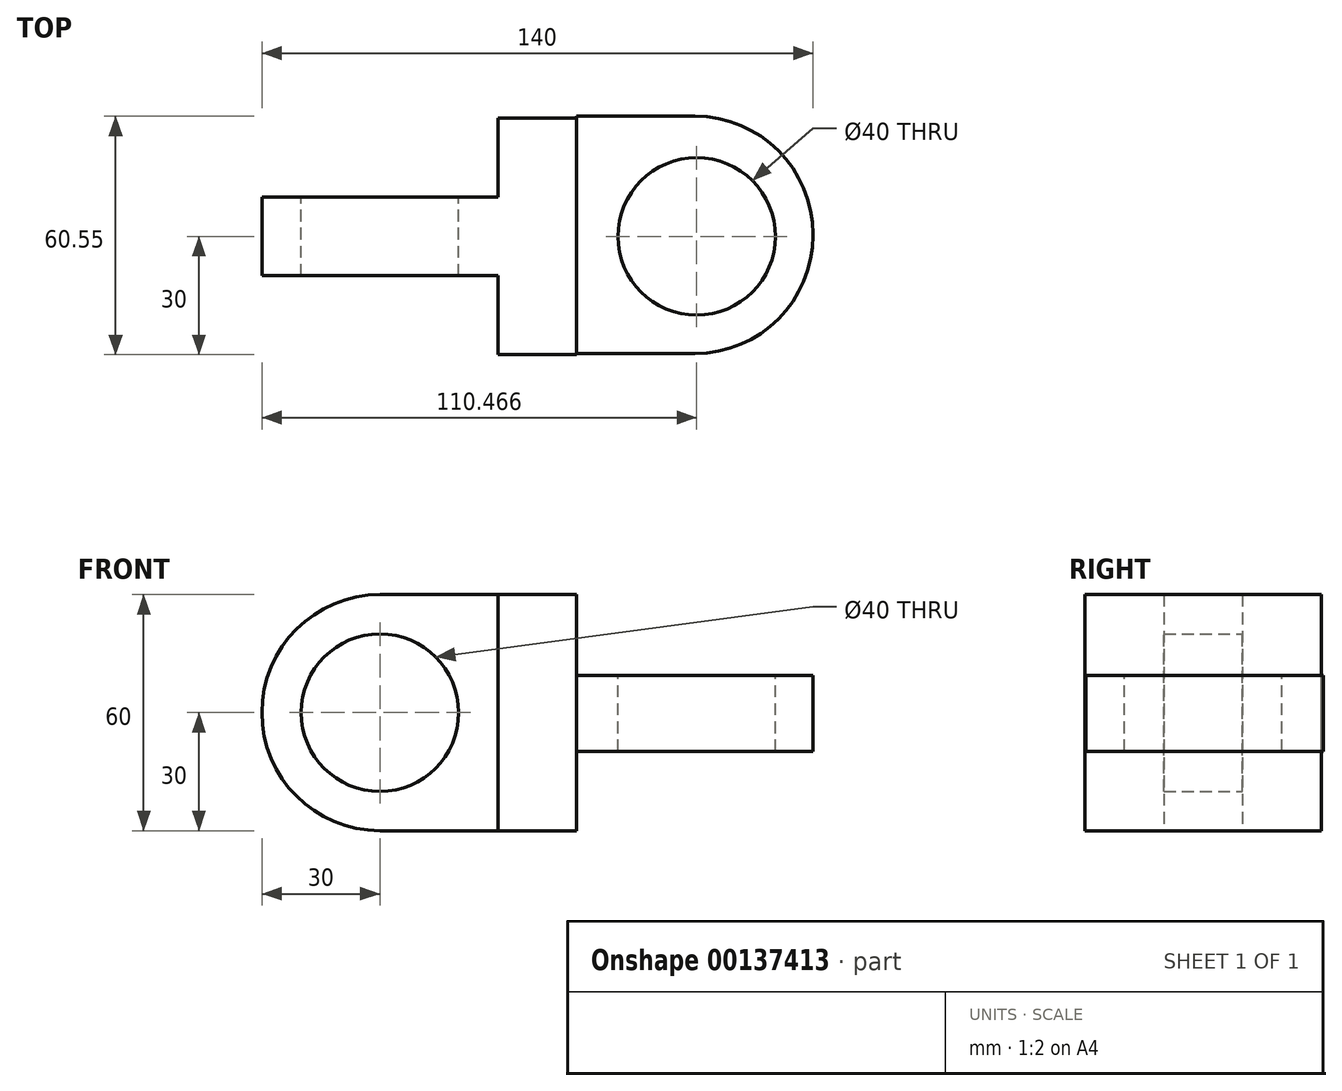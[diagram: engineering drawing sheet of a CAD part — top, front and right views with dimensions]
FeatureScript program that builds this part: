
annotation { "Feature Type Name" : "Feature", "Feature Type Description" : "" }
export const myFeature = defineFeature(function(context is Context, id is Id, definition is map)
    precondition{}
    {
        {
            var Q0;
            Q0=qCreatedBy(makeId("Front.planeOp"),FACE);
            var sketch = newSketch(context, id + "F8", { "sketchPlane" : qUnion([Q0])});
            skArc(sketch, "E0", {"start": v(0, 30) * mm, "mid": v(-30, 0) * mm, "end": v(0, -30) * mm});
            skCircle(sketch, "E1", {"center": v(0, 0) * mm, "radius": 20 * mm});
            skLineSegment(sketch, "E2", {"start": v(0, 30) * mm, "end": v(30, 30) * mm});
            skLineSegment(sketch, "E3", {"start": v(0, -30) * mm, "end": v(30, -30) * mm});
            skLineSegment(sketch, "E4", {"start": v(30, 30) * mm, "end": v(30, -30) * mm});
            skSolve(sketch);
        }
        {
            var Q0;
            {var subQ0=sQuery(id+"F8.wireOp",EDGE,"E2");Q0=makeQuery(id+"F8.imprint","IMPRINT",FACE,{"disambiguationData":[TD([[makeQuery(id+"F8.imprint","IMPRINT",EDGE,{"derivedFrom":subQ0}),-1.0]])]});}
            var Q1;
            Q1=makeQuery(id+"F8.imprint","IMPRINT",FACE,{"disambiguationData":[TD([[makeQuery(id+"F8.imprint","IMPRINT",EDGE,{"derivedFrom":sQuery(id+"F8.wireOp",EDGE,"E1")}),-1.0]])]});
            extrude(context, id + "F0", {"entities" : qUnion([Q0, Q1]), "depth" : 10 * mm, "hasSecondDirection" : true, "secondDirectionOppositeDirection" : true, "secondDirectionDepth" : 10 * mm});
        }
        {
            var Q0;
            Q0=makeQuery(id+"F0.opExtrude","SWEPT_FACE",FACE,{"disambiguationData":[OSD([sQuery(id+"F8.wireOp",EDGE,"E4")])]});
            var sketch = newSketch(context, id + "F1", { "sketchPlane" : qUnion([Q0])});
            skLineSegment(sketch, "E5", {"start": v(0, 30) * mm, "end": v(-30, 30) * mm});
            skLineSegment(sketch, "E6", {"start": v(0, 30) * mm, "end": v(30, 30) * mm});
            skLineSegment(sketch, "E7", {"start": v(-43.9, 0) * mm, "end": v(53.78, 0) * mm, "construction": true});
            skLineSegment(sketch, "E8.MirrorCS", {"start": v(0, -30) * mm, "end": v(30, -30) * mm});
            skLineSegment(sketch, "E9.MirrorCS", {"start": v(0, -30) * mm, "end": v(-30, -30) * mm});
            skLineSegment(sketch, "E10", {"start": v(30, -30) * mm, "end": v(30, 30) * mm});
            skLineSegment(sketch, "E11", {"start": v(-30, -30) * mm, "end": v(-30, 30) * mm});
            skSolve(sketch);
        }
        {
            var Q0;
            {var subQ2=sQuery(id+"F1.wireOp",EDGE,"E11");Q0=makeQuery(id+"F1.imprint","IMPRINT",FACE,{"disambiguationData":[TD([[makeQuery(id+"F1.imprint","IMPRINT",EDGE,{"derivedFrom":subQ2}),-1.0]])]});}
            var Q1;
            {var subQ2=sQuery(id+"F1.wireOp",EDGE,"E10");Q1=makeQuery(id+"F1.imprint","IMPRINT",FACE,{"disambiguationData":[TD([[makeQuery(id+"F1.imprint","IMPRINT",EDGE,{"derivedFrom":subQ2}),1.0]])]});}
            var Q2;
            {var subQ1=sQuery(id+"F8.wireOp",EDGE,"E4");var subQ5=makeQuery(id+"F0.opExtrude","CAP_EDGE",EDGE,{"disambiguationData":[OSD([subQ1])],"isStart":true});Q2=makeQuery(id+"F1.imprint","IMPRINT",FACE,{"disambiguationData":[TD([[makeQuery(id+"F1.imprint","IMPRINT",EDGE,{"derivedFrom":subQ5}),-1.0]])]});}
            extrude(context, id + "F2", {"entities" : qUnion([Q0, Q1, Q2]), "operationType" : NewBodyOperationType.ADD, "depth" : 20 * mm});
        }
        {
            var Q0;
            Q0=qCreatedBy(makeId("Right.planeOp"),FACE);
            cPlane(context, id + "F3", {"entities" : qUnion([Q0]), "cplaneType" : CPlaneType.OFFSET, "offset" : 40 * mm, "width" : 150 * mm, "height" : 150 * mm});
        }
        {
            var Q0;
            Q0=qCreatedBy(id+"F3.planeOp",FACE);
            cPlane(context, id + "F4", {"entities" : qUnion([Q0]), "cplaneType" : CPlaneType.OFFSET, "offset" : 10 * mm, "width" : 150 * mm, "height" : 150 * mm});
        }
        {
            var Q0;
            Q0=qCreatedBy(id+"F4.planeOp",FACE);
            var sketch = newSketch(context, id + "F5", { "sketchPlane" : qUnion([Q0])});
            skLineSegment(sketch, "E12", {"start": v(-29.77, -0.54) * mm, "end": v(-29.77, 9.46) * mm});
            skLineSegment(sketch, "E13", {"start": v(-29.77, -0.54) * mm, "end": v(-29.77, -9.83) * mm});
            skLineSegment(sketch, "E14", {"start": v(-29.77, 9.46) * mm, "end": v(30.55, 9.46) * mm});
            skLineSegment(sketch, "E15", {"start": v(30.55, 9.46) * mm, "end": v(30.55, -9.83) * mm});
            skLineSegment(sketch, "E16", {"start": v(30.55, -9.83) * mm, "end": v(-29.77, -9.83) * mm});
            skSolve(sketch);
        }
        {
            var Q0;
            Q0=makeQuery(id+"F5.imprint","IMPRINT",FACE,{"disambiguationData":[TD([[makeQuery(id+"F5.imprint","IMPRINT",EDGE,{"derivedFrom":sQuery(id+"F5.wireOp",EDGE,"E12")}),-1.0]])]});
            extrude(context, id + "F9", {"entities" : qUnion([Q0]), "operationType" : NewBodyOperationType.ADD, "depth" : 60 * mm});
        }
        {
            var Q0;
            Q0=makeQuery(id+"F9.opExtrude","SWEPT_FACE",FACE,{"disambiguationData":[OSD([sQuery(id+"F5.wireOp",EDGE,"E14")])]});
            var sketch = newSketch(context, id + "F6", { "sketchPlane" : qUnion([Q0])});
            skCircle(sketch, "E17", {"center": v(80.47, 0) * mm, "radius": 20 * mm});
            skSolve(sketch);
        }
        {
            var Q0;
            Q0=makeQuery(id+"F6.imprint","IMPRINT",FACE,{"disambiguationData":[TD([[makeQuery(id+"F6.imprint","IMPRINT",EDGE,{"derivedFrom":sQuery(id+"F6.wireOp",EDGE,"E17")}),1.0]])]});
            extrude(context, id + "F10", {"entities" : qUnion([Q0]), "operationType" : NewBodyOperationType.REMOVE, "oppositeDirection" : true, "depth" : 25 * mm});
        }
        {
            var Q0;
            Q0=makeQuery(id+"F9.opExtrude","CAP_EDGE",EDGE,{"disambiguationData":[OSD([sQuery(id+"F5.wireOp",EDGE,"E12"),sQuery(id+"F5.wireOp",EDGE,"E13")])],"isStart":false});
            var Q1;
            Q1=makeQuery(id+"F9.opExtrude","CAP_EDGE",EDGE,{"disambiguationData":[OSD([sQuery(id+"F5.wireOp",EDGE,"E15")])],"isStart":false});
            fillet(context, id + "F7", {"entities" : qUnion([Q0, Q1]), "radius" : 30 * mm, "tangentPropagation" : true, "allowEdgeOverflow" : false});
        }
    });
